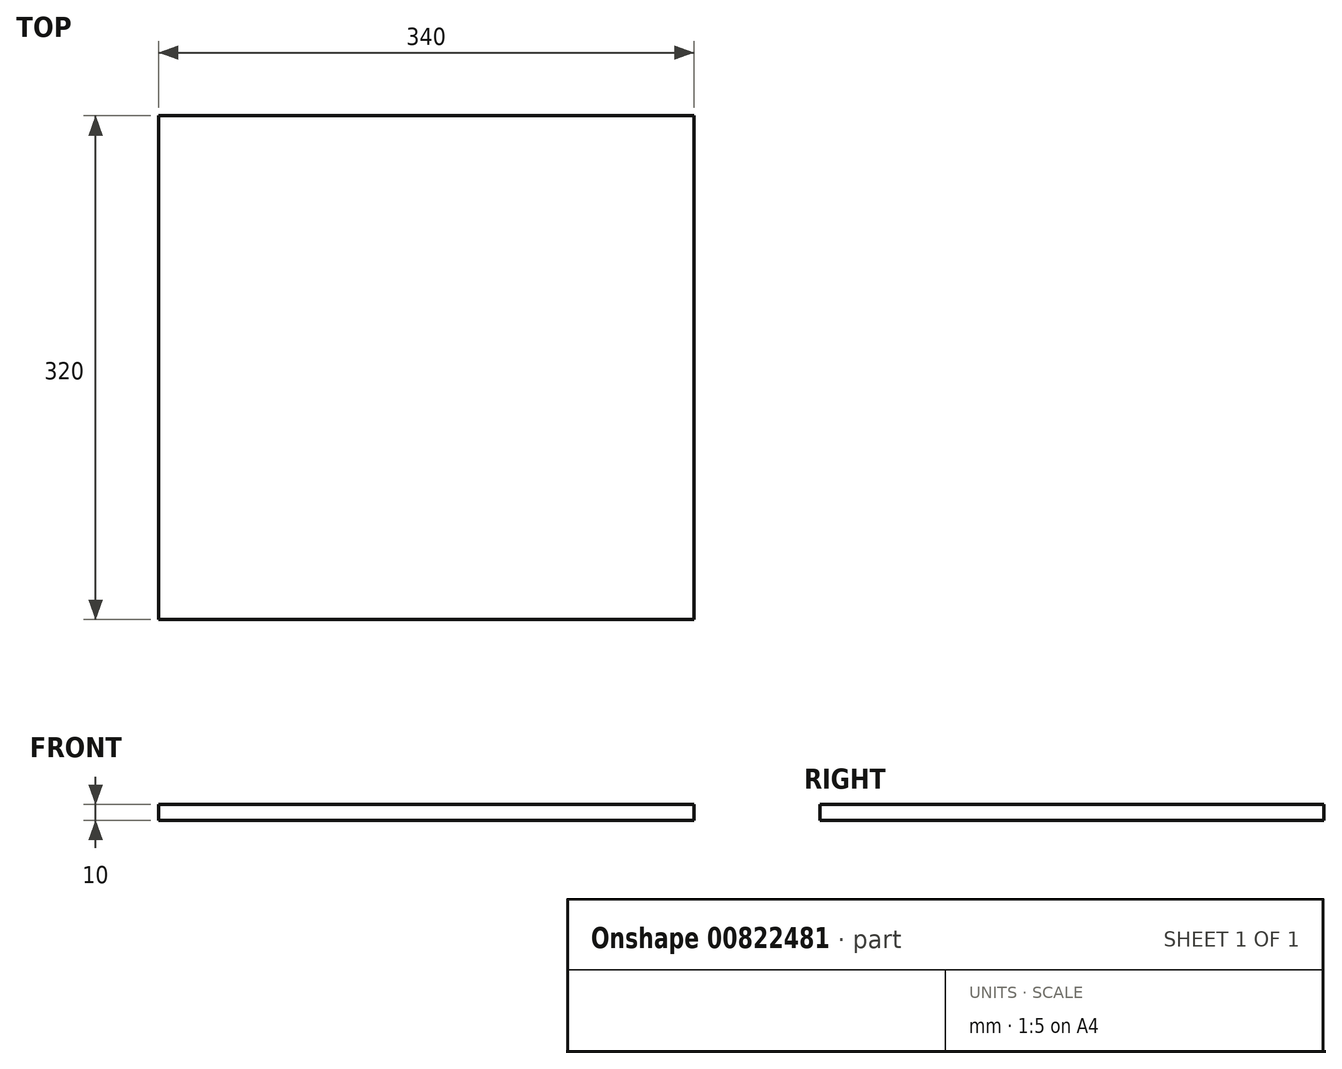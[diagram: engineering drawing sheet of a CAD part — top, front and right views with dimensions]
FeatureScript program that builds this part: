
annotation { "Feature Type Name" : "Feature", "Feature Type Description" : "" }
export const myFeature = defineFeature(function(context is Context, id is Id, definition is map)
    precondition{}
    {
        {
            var Q0;
            Q0=qCreatedBy(makeId("Top.planeOp"),FACE);
            var sketch = newSketch(context, id + "F0", { "sketchPlane" : qUnion([Q0])});
            skLineSegment(sketch, "E0.bottom", {"start": v(-170, 160.82) * mm, "end": v(170, 160.82) * mm});
            skLineSegment(sketch, "E0.top", {"start": v(-170, -159.18) * mm, "end": v(170, -159.18) * mm});
            skLineSegment(sketch, "E0.left", {"start": v(-170, 160.82) * mm, "end": v(-170, -159.18) * mm});
            skLineSegment(sketch, "E0.right", {"start": v(170, 160.82) * mm, "end": v(170, -159.18) * mm});
            skSolve(sketch);
        }
        {
            var Q0;
            Q0=makeQuery(id+"F0.imprint","IMPRINT",FACE,{"disambiguationData":[TD([[makeQuery(id+"F0.imprint","IMPRINT",EDGE,{"derivedFrom":sQuery(id+"F0.wireOp",EDGE,"E0.bottom")}),-1.0]])]});
            extrude(context, id + "F1", {"entities" : qUnion([Q0]), "depth" : 10 * mm, "offsetDistance" : 25.4 * mm});
        }
    });
